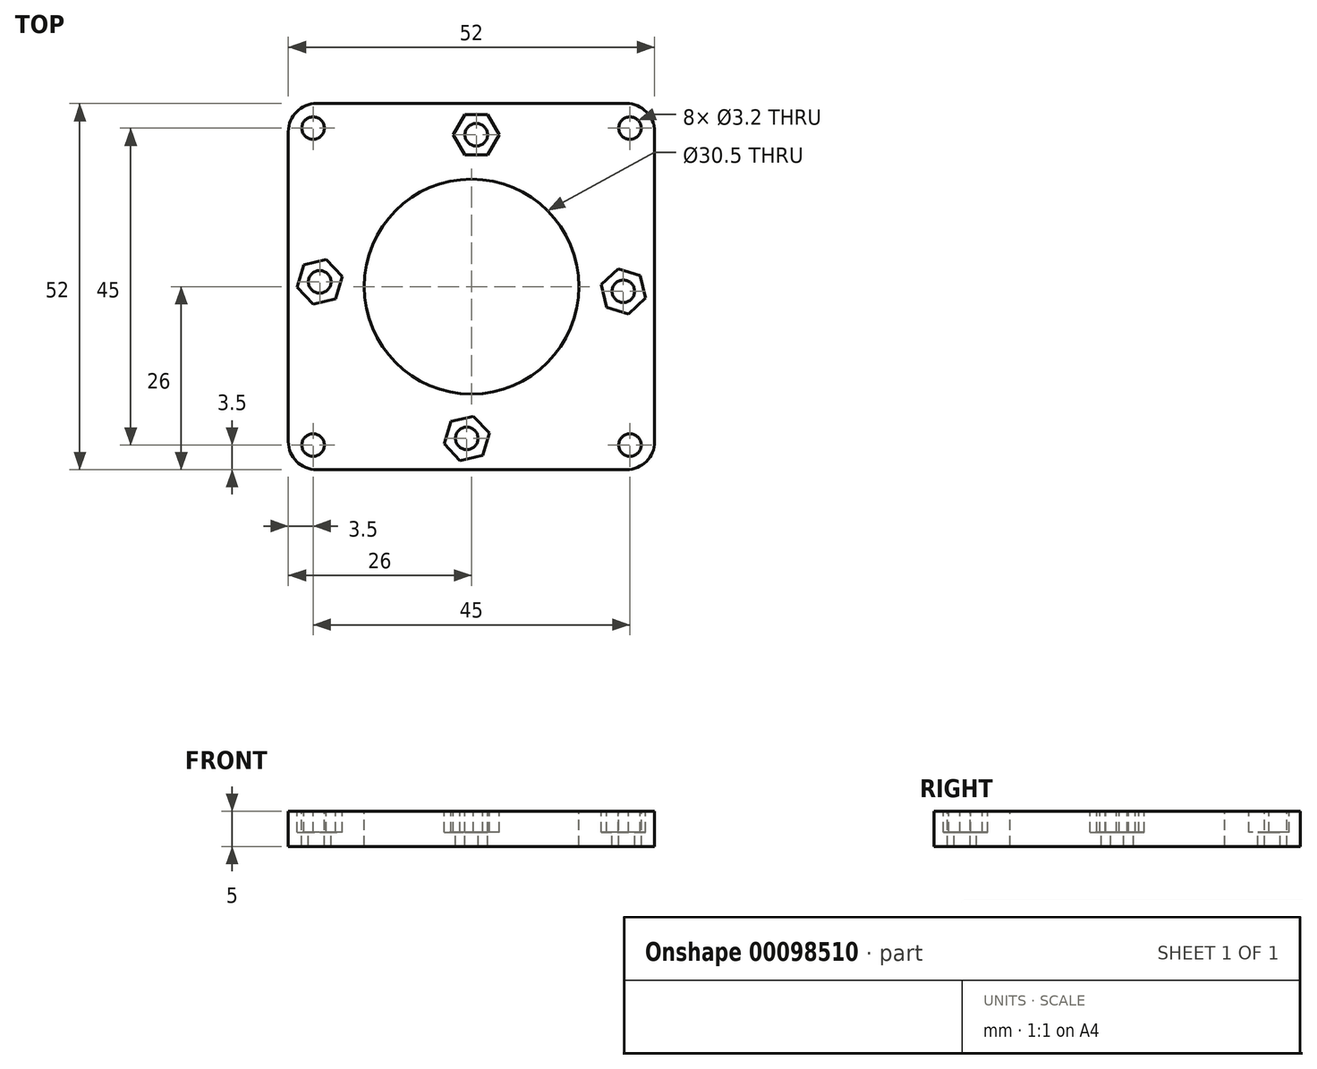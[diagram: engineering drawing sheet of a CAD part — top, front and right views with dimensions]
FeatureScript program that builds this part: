
annotation { "Feature Type Name" : "Feature", "Feature Type Description" : "" }
export const myFeature = defineFeature(function(context is Context, id is Id, definition is map)
    precondition{}
    {
        {
            var Q0;
            Q0=qCreatedBy(makeId("Top.planeOp"),FACE);
            var sketch = newSketch(context, id + "F0", { "sketchPlane" : qUnion([Q0])});
            skLineSegment(sketch, "E0.bottom", {"start": v(22.5, 22.5) * mm, "end": v(-22.5, 22.5) * mm, "construction": true});
            skLineSegment(sketch, "E0.top", {"start": v(22.5, -22.5) * mm, "end": v(-22.5, -22.5) * mm, "construction": true});
            skLineSegment(sketch, "E0.left", {"start": v(22.5, 22.5) * mm, "end": v(22.5, -22.5) * mm, "construction": true});
            skLineSegment(sketch, "E0.right", {"start": v(-22.5, 22.5) * mm, "end": v(-22.5, -22.5) * mm, "construction": true});
            skPoint(sketch, "E0.middle", {"position": v(0, 0) * mm});
            skCircle(sketch, "E1", {"center": v(-22.5, 22.5) * mm, "radius": 1.6 * mm});
            skCircle(sketch, "E2", {"center": v(22.5, 22.5) * mm, "radius": 1.6 * mm});
            skCircle(sketch, "E3", {"center": v(22.5, -22.5) * mm, "radius": 1.6 * mm});
            skCircle(sketch, "E4", {"center": v(-22.5, -22.5) * mm, "radius": 1.6 * mm});
            skLineSegment(sketch, "E5.bottom", {"start": v(26, 26) * mm, "end": v(-26, 26) * mm});
            skLineSegment(sketch, "E5.top", {"start": v(26, -26) * mm, "end": v(-26, -26) * mm});
            skLineSegment(sketch, "E5.left", {"start": v(26, 26) * mm, "end": v(26, -26) * mm});
            skLineSegment(sketch, "E5.right", {"start": v(-26, 26) * mm, "end": v(-26, -26) * mm});
            skCircle(sketch, "E6", {"center": v(0, 0) * mm, "radius": 15.25 * mm});
            skLineSegment(sketch, "E7", {"start": v(0, 0) * mm, "end": v(15.25, 0) * mm});
            skLineSegment(sketch, "E8", {"start": v(0, 0) * mm, "end": v(11.11, 10.44) * mm});
            skLineSegment(sketch, "E9", {"start": v(0, 0) * mm, "end": v(-10.44, 11.11) * mm});
            skLineSegment(sketch, "E10", {"start": v(0, 0) * mm, "end": v(10.44, -11.11) * mm});
            skCircle(sketch, "E11.cCircle", {"center": v(0, 0) * mm, "radius": 15.25 * mm, "construction": true});
            skLineSegment(sketch, "E11.0", {"start": v(-21.56, 0.67) * mm, "end": v(0.67, 21.56) * mm});
            skLineSegment(sketch, "E11.1", {"start": v(0.67, 21.56) * mm, "end": v(21.56, -0.67) * mm});
            skLineSegment(sketch, "E11.2", {"start": v(21.56, -0.67) * mm, "end": v(-0.67, -21.56) * mm});
            skLineSegment(sketch, "E11.3", {"start": v(-0.67, -21.56) * mm, "end": v(-21.56, 0.67) * mm});
            skPoint(sketch, "E11.0.midPoint", {"position": v(-10.44, 11.11) * mm});
            skCircle(sketch, "E12", {"center": v(-21.56, 0.67) * mm, "radius": 1.6 * mm});
            skCircle(sketch, "E13", {"center": v(-0.67, -21.56) * mm, "radius": 1.6 * mm});
            skCircle(sketch, "E14", {"center": v(21.56, -0.67) * mm, "radius": 1.6 * mm});
            skCircle(sketch, "E15", {"center": v(0.67, 21.56) * mm, "radius": 1.6 * mm});
            skCircle(sketch, "E16.cCircle", {"center": v(21.56, -0.67) * mm, "radius": 2.85 * mm, "construction": true});
            skLineSegment(sketch, "E16.0", {"start": v(18.4, 0.28) * mm, "end": v(20.8, 2.53) * mm});
            skLineSegment(sketch, "E16.1", {"start": v(20.8, 2.53) * mm, "end": v(23.95, 1.58) * mm});
            skLineSegment(sketch, "E16.2", {"start": v(23.95, 1.58) * mm, "end": v(24.7, -1.62) * mm});
            skLineSegment(sketch, "E16.3", {"start": v(24.7, -1.62) * mm, "end": v(22.3, -3.88) * mm});
            skLineSegment(sketch, "E16.4", {"start": v(22.3, -3.88) * mm, "end": v(19.16, -2.93) * mm});
            skLineSegment(sketch, "E16.5", {"start": v(19.16, -2.93) * mm, "end": v(18.4, 0.28) * mm});
            skPoint(sketch, "E16.0.midPoint", {"position": v(19.6, 1.4) * mm});
            skCircle(sketch, "E17.cCircle", {"center": v(-0.67, -21.56) * mm, "radius": 2.85 * mm, "construction": true});
            skLineSegment(sketch, "E17.0", {"start": v(0.28, -18.4) * mm, "end": v(2.53, -20.8) * mm});
            skLineSegment(sketch, "E17.1", {"start": v(2.53, -20.8) * mm, "end": v(1.58, -23.95) * mm});
            skLineSegment(sketch, "E17.2", {"start": v(1.58, -23.95) * mm, "end": v(-1.62, -24.7) * mm});
            skLineSegment(sketch, "E17.3", {"start": v(-1.62, -24.7) * mm, "end": v(-3.88, -22.3) * mm});
            skLineSegment(sketch, "E17.4", {"start": v(-3.88, -22.3) * mm, "end": v(-2.93, -19.16) * mm});
            skLineSegment(sketch, "E17.5", {"start": v(-2.93, -19.16) * mm, "end": v(0.28, -18.4) * mm});
            skPoint(sketch, "E17.0.midPoint", {"position": v(1.4, -19.6) * mm});
            skCircle(sketch, "E18.cCircle", {"center": v(-21.56, 0.67) * mm, "radius": 2.85 * mm, "construction": true});
            skLineSegment(sketch, "E18.0", {"start": v(-20.6, 3.82) * mm, "end": v(-18.35, 1.42) * mm});
            skLineSegment(sketch, "E18.1", {"start": v(-18.35, 1.42) * mm, "end": v(-19.3, -1.73) * mm});
            skLineSegment(sketch, "E18.2", {"start": v(-19.3, -1.73) * mm, "end": v(-22.5, -2.48) * mm});
            skLineSegment(sketch, "E18.3", {"start": v(-22.5, -2.48) * mm, "end": v(-24.76, -0.08) * mm});
            skLineSegment(sketch, "E18.4", {"start": v(-24.76, -0.08) * mm, "end": v(-23.8, 3.07) * mm});
            skLineSegment(sketch, "E18.5", {"start": v(-23.8, 3.07) * mm, "end": v(-20.6, 3.82) * mm});
            skPoint(sketch, "E18.0.midPoint", {"position": v(-19.48, 2.62) * mm});
            skCircle(sketch, "E19.cCircle", {"center": v(0.67, 21.56) * mm, "radius": 2.85 * mm, "construction": true});
            skLineSegment(sketch, "E19.0", {"start": v(2.32, 18.7) * mm, "end": v(-0.97, 18.7) * mm});
            skLineSegment(sketch, "E19.1", {"start": v(-0.97, 18.7) * mm, "end": v(-2.62, 21.56) * mm});
            skLineSegment(sketch, "E19.2", {"start": v(-2.62, 21.56) * mm, "end": v(-0.97, 24.4) * mm});
            skLineSegment(sketch, "E19.3", {"start": v(-0.97, 24.4) * mm, "end": v(2.32, 24.4) * mm});
            skLineSegment(sketch, "E19.4", {"start": v(2.32, 24.4) * mm, "end": v(3.96, 21.56) * mm});
            skLineSegment(sketch, "E19.5", {"start": v(3.96, 21.56) * mm, "end": v(2.32, 18.7) * mm});
            skPoint(sketch, "E19.0.midPoint", {"position": v(0.67, 18.7) * mm});
            skSolve(sketch);
        }
        {
            var Q0;
            Q0=makeQuery(id+"F0.imprint","IMPRINT",FACE,{"disambiguationData":[TD([[makeQuery(id+"F0.imprint","IMPRINT",EDGE,{"derivedFrom":sQuery(id+"F0.wireOp",EDGE,"E5.bottom")}),1.0]])]});
            var Q1;
            {var subQ21=sQuery(id+"F0.wireOp",EDGE,"7e4dd14e-6d11-4e82-8602-8d45d74979fb.2");Q1=makeQuery(id+"F0.imprint","IMPRINT",FACE,{"disambiguationData":[TD([[makeQuery(id+"F0.imprint","IMPRINT",EDGE,{"derivedFrom":subQ21}),1.0]])]});}
            var Q2;
            {var subQ0=sQuery(id+"F0.wireOp",EDGE,"7e4dd14e-6d11-4e82-8602-8d45d74979fb.1");Q2=makeQuery(id+"F0.imprint","IMPRINT",FACE,{"disambiguationData":[TD([[makeQuery(id+"F0.imprint","IMPRINT",EDGE,{"derivedFrom":subQ0}),1.0]])]});}
            var Q3;
            {var subQ0=sQuery(id+"F0.wireOp",EDGE,"995da377-a2e7-4e52-8412-fc9ad2e70efc.5");Q3=makeQuery(id+"F0.imprint","IMPRINT",FACE,{"disambiguationData":[TD([[makeQuery(id+"F0.imprint","IMPRINT",EDGE,{"derivedFrom":subQ0}),1.0]])]});}
            var Q4;
            {var subQ0=sQuery(id+"F0.wireOp",EDGE,"2f8e4698-9220-4ba4-a292-a56cc426eeca.1");Q4=makeQuery(id+"F0.imprint","IMPRINT",FACE,{"disambiguationData":[TD([[makeQuery(id+"F0.imprint","IMPRINT",EDGE,{"derivedFrom":subQ0}),1.0]])]});}
            var Q5;
            {var subQ5=sQuery(id+"F0.wireOp",EDGE,"c89aa8a5-abf0-4b07-8778-4629d9170b15.5");Q5=makeQuery(id+"F0.imprint","IMPRINT",FACE,{"disambiguationData":[TD([[makeQuery(id+"F0.imprint","IMPRINT",EDGE,{"derivedFrom":subQ5}),1.0]])]});}
            var Q6;
            {var subQ0=sQuery(id+"F0.wireOp",EDGE,"995da377-a2e7-4e52-8412-fc9ad2e70efc.1");Q6=makeQuery(id+"F0.imprint","IMPRINT",FACE,{"disambiguationData":[TD([[makeQuery(id+"F0.imprint","IMPRINT",EDGE,{"derivedFrom":subQ0}),-1.0]])]});}
            var Q7;
            {var subQ0=sQuery(id+"F0.wireOp",EDGE,"995da377-a2e7-4e52-8412-fc9ad2e70efc.5");Q7=makeQuery(id+"F0.imprint","IMPRINT",FACE,{"disambiguationData":[TD([[makeQuery(id+"F0.imprint","IMPRINT",EDGE,{"derivedFrom":subQ0}),-1.0]])]});}
            var Q8;
            {var subQ5=sQuery(id+"F0.wireOp",EDGE,"7e4dd14e-6d11-4e82-8602-8d45d74979fb.1");Q8=makeQuery(id+"F0.imprint","IMPRINT",FACE,{"disambiguationData":[TD([[makeQuery(id+"F0.imprint","IMPRINT",EDGE,{"derivedFrom":subQ5}),-1.0]])]});}
            var Q9;
            {var subQ8=sQuery(id+"F0.wireOp",EDGE,"7e4dd14e-6d11-4e82-8602-8d45d74979fb.2");Q9=makeQuery(id+"F0.imprint","IMPRINT",FACE,{"disambiguationData":[TD([[makeQuery(id+"F0.imprint","IMPRINT",EDGE,{"derivedFrom":subQ8}),-1.0]])]});}
            var Q10;
            {var subQ5=sQuery(id+"F0.wireOp",EDGE,"c89aa8a5-abf0-4b07-8778-4629d9170b15.1");Q10=makeQuery(id+"F0.imprint","IMPRINT",FACE,{"disambiguationData":[TD([[makeQuery(id+"F0.imprint","IMPRINT",EDGE,{"derivedFrom":subQ5}),-1.0]])]});}
            var Q11;
            {var subQ5=sQuery(id+"F0.wireOp",EDGE,"c89aa8a5-abf0-4b07-8778-4629d9170b15.5");Q11=makeQuery(id+"F0.imprint","IMPRINT",FACE,{"disambiguationData":[TD([[makeQuery(id+"F0.imprint","IMPRINT",EDGE,{"derivedFrom":subQ5}),-1.0]])]});}
            var Q12;
            {var subQ8=sQuery(id+"F0.wireOp",EDGE,"2f8e4698-9220-4ba4-a292-a56cc426eeca.2");Q12=makeQuery(id+"F0.imprint","IMPRINT",FACE,{"disambiguationData":[TD([[makeQuery(id+"F0.imprint","IMPRINT",EDGE,{"derivedFrom":subQ8}),-1.0]])]});}
            var Q13;
            {var subQ5=sQuery(id+"F0.wireOp",EDGE,"2f8e4698-9220-4ba4-a292-a56cc426eeca.1");Q13=makeQuery(id+"F0.imprint","IMPRINT",FACE,{"disambiguationData":[TD([[makeQuery(id+"F0.imprint","IMPRINT",EDGE,{"derivedFrom":subQ5}),-1.0]])]});}
            var Q14;
            {var subQ0=sQuery(id+"F0.wireOp",EDGE,"E19.0");Q14=makeQuery(id+"F0.imprint","IMPRINT",FACE,{"disambiguationData":[TD([[makeQuery(id+"F0.imprint","IMPRINT",EDGE,{"derivedFrom":subQ0}),1.0]])]});}
            var Q15;
            {var subQ3=sQuery(id+"F0.wireOp",EDGE,"E16.5");Q15=makeQuery(id+"F0.imprint","IMPRINT",FACE,{"disambiguationData":[TD([[makeQuery(id+"F0.imprint","IMPRINT",EDGE,{"derivedFrom":subQ3}),1.0]])]});}
            var Q16;
            {var subQ0=sQuery(id+"F0.wireOp",EDGE,"E17.5");Q16=makeQuery(id+"F0.imprint","IMPRINT",FACE,{"disambiguationData":[TD([[makeQuery(id+"F0.imprint","IMPRINT",EDGE,{"derivedFrom":subQ0}),1.0]])]});}
            var Q17;
            {var subQ0=sQuery(id+"F0.wireOp",EDGE,"E18.1");Q17=makeQuery(id+"F0.imprint","IMPRINT",FACE,{"disambiguationData":[TD([[makeQuery(id+"F0.imprint","IMPRINT",EDGE,{"derivedFrom":subQ0}),1.0]])]});}
            var Q18;
            {var subQ0=sQuery(id+"F0.wireOp",EDGE,"E18.1");Q18=makeQuery(id+"F0.imprint","IMPRINT",FACE,{"disambiguationData":[TD([[makeQuery(id+"F0.imprint","IMPRINT",EDGE,{"derivedFrom":subQ0}),-1.0]])]});}
            var Q19;
            {var subQ4=sQuery(id+"F0.wireOp",EDGE,"E18.2");Q19=makeQuery(id+"F0.imprint","IMPRINT",FACE,{"disambiguationData":[TD([[makeQuery(id+"F0.imprint","IMPRINT",EDGE,{"derivedFrom":subQ4}),-1.0]])]});}
            var Q20;
            {var subQ0=sQuery(id+"F0.wireOp",EDGE,"E19.2");Q20=makeQuery(id+"F0.imprint","IMPRINT",FACE,{"disambiguationData":[TD([[makeQuery(id+"F0.imprint","IMPRINT",EDGE,{"derivedFrom":subQ0}),-1.0]])]});}
            var Q21;
            {var subQ0=sQuery(id+"F0.wireOp",EDGE,"E19.0");Q21=makeQuery(id+"F0.imprint","IMPRINT",FACE,{"disambiguationData":[TD([[makeQuery(id+"F0.imprint","IMPRINT",EDGE,{"derivedFrom":subQ0}),-1.0]])]});}
            var Q22;
            {var subQ0=sQuery(id+"F0.wireOp",EDGE,"E16.5");Q22=makeQuery(id+"F0.imprint","IMPRINT",FACE,{"disambiguationData":[TD([[makeQuery(id+"F0.imprint","IMPRINT",EDGE,{"derivedFrom":subQ0}),-1.0]])]});}
            var Q23;
            {var subQ0=sQuery(id+"F0.wireOp",EDGE,"E16.1");Q23=makeQuery(id+"F0.imprint","IMPRINT",FACE,{"disambiguationData":[TD([[makeQuery(id+"F0.imprint","IMPRINT",EDGE,{"derivedFrom":subQ0}),-1.0]])]});}
            var Q24;
            {var subQ0=sQuery(id+"F0.wireOp",EDGE,"E17.1");Q24=makeQuery(id+"F0.imprint","IMPRINT",FACE,{"disambiguationData":[TD([[makeQuery(id+"F0.imprint","IMPRINT",EDGE,{"derivedFrom":subQ0}),-1.0]])]});}
            var Q25;
            {var subQ0=sQuery(id+"F0.wireOp",EDGE,"E17.5");Q25=makeQuery(id+"F0.imprint","IMPRINT",FACE,{"disambiguationData":[TD([[makeQuery(id+"F0.imprint","IMPRINT",EDGE,{"derivedFrom":subQ0}),-1.0]])]});}
            extrude(context, id + "F1", {"entities" : qUnion([Q0, Q1, Q2, Q3, Q4, Q5, Q6, Q7, Q8, Q9, Q10, Q11, Q12, Q13, Q14, Q15, Q16, Q17, Q18, Q19, Q20, Q21, Q22, Q23, Q24, Q25]), "oppositeDirection" : true, "depth" : 5 * mm});
        }
        {
            var Q0;
            {var subQ4=sQuery(id+"F0.wireOp",EDGE,"E18.2");Q0=makeQuery(id+"F0.imprint","IMPRINT",FACE,{"disambiguationData":[TD([[makeQuery(id+"F0.imprint","IMPRINT",EDGE,{"derivedFrom":subQ4}),-1.0]])]});}
            var Q1;
            {var subQ0=sQuery(id+"F0.wireOp",EDGE,"E18.1");Q1=makeQuery(id+"F0.imprint","IMPRINT",FACE,{"disambiguationData":[TD([[makeQuery(id+"F0.imprint","IMPRINT",EDGE,{"derivedFrom":subQ0}),-1.0]])]});}
            var Q2;
            {var subQ0=sQuery(id+"F0.wireOp",EDGE,"E19.0");Q2=makeQuery(id+"F0.imprint","IMPRINT",FACE,{"disambiguationData":[TD([[makeQuery(id+"F0.imprint","IMPRINT",EDGE,{"derivedFrom":subQ0}),-1.0]])]});}
            var Q3;
            {var subQ0=sQuery(id+"F0.wireOp",EDGE,"E19.2");Q3=makeQuery(id+"F0.imprint","IMPRINT",FACE,{"disambiguationData":[TD([[makeQuery(id+"F0.imprint","IMPRINT",EDGE,{"derivedFrom":subQ0}),-1.0]])]});}
            var Q4;
            {var subQ0=sQuery(id+"F0.wireOp",EDGE,"E16.5");Q4=makeQuery(id+"F0.imprint","IMPRINT",FACE,{"disambiguationData":[TD([[makeQuery(id+"F0.imprint","IMPRINT",EDGE,{"derivedFrom":subQ0}),-1.0]])]});}
            var Q5;
            {var subQ0=sQuery(id+"F0.wireOp",EDGE,"E16.1");Q5=makeQuery(id+"F0.imprint","IMPRINT",FACE,{"disambiguationData":[TD([[makeQuery(id+"F0.imprint","IMPRINT",EDGE,{"derivedFrom":subQ0}),-1.0]])]});}
            var Q6;
            {var subQ0=sQuery(id+"F0.wireOp",EDGE,"E17.5");Q6=makeQuery(id+"F0.imprint","IMPRINT",FACE,{"disambiguationData":[TD([[makeQuery(id+"F0.imprint","IMPRINT",EDGE,{"derivedFrom":subQ0}),-1.0]])]});}
            var Q7;
            {var subQ0=sQuery(id+"F0.wireOp",EDGE,"E17.1");Q7=makeQuery(id+"F0.imprint","IMPRINT",FACE,{"disambiguationData":[TD([[makeQuery(id+"F0.imprint","IMPRINT",EDGE,{"derivedFrom":subQ0}),-1.0]])]});}
            extrude(context, id + "F2", {"entities" : qUnion([Q0, Q1, Q2, Q3, Q4, Q5, Q6, Q7]), "operationType" : NewBodyOperationType.REMOVE, "oppositeDirection" : true, "depth" : 3 * mm});
        }
        {
            var Q0;
            Q0=makeQuery(id+"F1.opExtrude","SWEPT_EDGE",EDGE,{"disambiguationData":[OSD([sQuery(id+"F0.wireOp",EDGE,"E5.top"),sQuery(id+"F0.wireOp",EDGE,"E5.right")])]});
            var Q1;
            Q1=makeQuery(id+"F1.opExtrude","SWEPT_EDGE",EDGE,{"disambiguationData":[OSD([sQuery(id+"F0.wireOp",EDGE,"E5.top"),sQuery(id+"F0.wireOp",EDGE,"E5.left")])]});
            var Q2;
            Q2=makeQuery(id+"F1.opExtrude","SWEPT_EDGE",EDGE,{"disambiguationData":[OSD([sQuery(id+"F0.wireOp",EDGE,"E5.bottom"),sQuery(id+"F0.wireOp",EDGE,"E5.right")])]});
            var Q3;
            Q3=makeQuery(id+"F1.opExtrude","SWEPT_EDGE",EDGE,{"disambiguationData":[OSD([sQuery(id+"F0.wireOp",EDGE,"E5.bottom"),sQuery(id+"F0.wireOp",EDGE,"E5.left")])]});
            fillet(context, id + "F3", {"entities" : qUnion([Q0, Q1, Q2, Q3]), "radius" : 4 * mm, "tangentPropagation" : true, "allowEdgeOverflow" : false});
        }
    });
